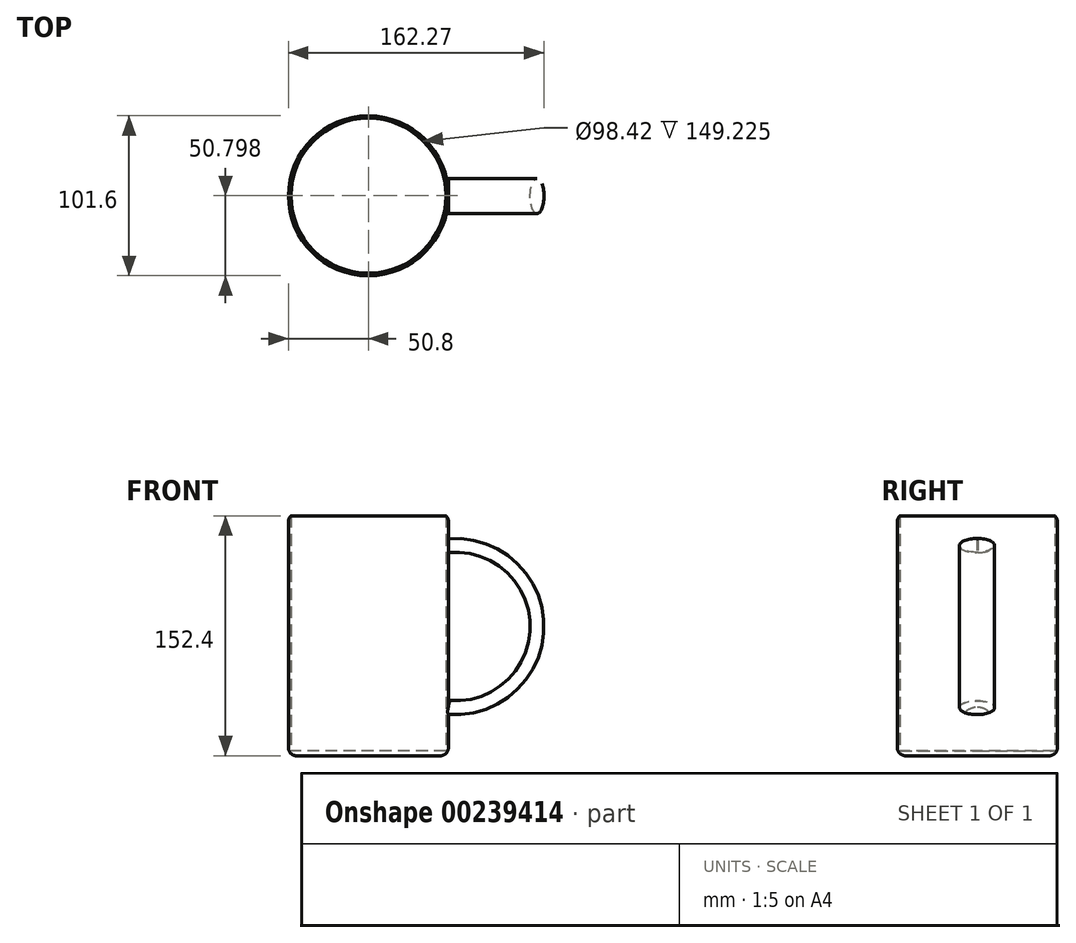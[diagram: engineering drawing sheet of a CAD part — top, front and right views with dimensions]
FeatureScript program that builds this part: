
annotation { "Feature Type Name" : "Feature", "Feature Type Description" : "" }
export const myFeature = defineFeature(function(context is Context, id is Id, definition is map)
    precondition{}
    {
        {
            var Q0;
            Q0=qCreatedBy(makeId("Top.planeOp"),FACE);
            var sketch = newSketch(context, id + "F0", { "sketchPlane" : qUnion([Q0])});
            skCircle(sketch, "E0", {"center": v(-50.8, 0.22) * mm, "radius": 50.8 * mm});
            skPoint(sketch, "E0.first.point", {"position": v(0, 0) * mm});
            skPoint(sketch, "E0.second.point", {"position": v(-101.53, -2.37) * mm});
            skPoint(sketch, "E0.third.point", {"position": v(-78.18, -42.57) * mm});
            skCircle(sketch, "E1", {"center": v(-50.8, 0.22) * mm, "radius": 49.21 * mm});
            skSolve(sketch);
        }
        {
            var Q0;
            Q0 = qSketchRegion(id + "F0", true);
            extrude(context, id + "F1", {"entities" : qUnion([Q0]), "depth" : 152.4 * mm});
        }
        {
            var Q0;
            Q0=makeQuery(id+"F0.imprint","IMPRINT",FACE,{"disambiguationData":[TD([[makeQuery(id+"F0.imprint","IMPRINT",EDGE,{"derivedFrom":sQuery(id+"F0.wireOp",EDGE,"E1")}),1.0]])]});
            extrude(context, id + "F2", {"entities" : qUnion([Q0]), "operationType" : NewBodyOperationType.ADD, "depth" : 3.17 * mm});
        }
        {
            var Q0;
            Q0=qCreatedBy(makeId("Right.planeOp"),FACE);
            var sketch = newSketch(context, id + "F3", { "sketchPlane" : qUnion([Q0])});
            skEllipse(sketch, "E2", {"center": v(0, 133.4) * mm, "majorRadius": 11.13 * mm, "minorRadius": 4.4 * mm, "majorAxis": v(1, 0)});
            skEllipse(sketch, "E3", {"center": v(0.27, 30.77) * mm, "majorRadius": 11.13 * mm, "minorRadius": 4.4 * mm, "majorAxis": v(1, 0)});
            skSolve(sketch);
        }
        {
            var Q0;
            Q0=qCreatedBy(makeId("Front.planeOp"),FACE);
            var sketch = newSketch(context, id + "F4", { "sketchPlane" : qUnion([Q0])});
            skArc(sketch, "E4", {"start": v(0, 31.04) * mm, "mid": v(56.02, 82.09) * mm, "end": v(0, 133.13) * mm});
            skSolve(sketch);
        }
        {
            var Q0;
            Q0=makeQuery(id+"F3.imprint","IMPRINT",FACE,{"disambiguationData":[TD([[makeQuery(id+"F3.imprint","IMPRINT",EDGE,{"derivedFrom":sQuery(id+"F3.wireOp",EDGE,"E2")}),1.0]])]});
            var Q1;
            Q1=sQuery(id+"F4.wireOp",EDGE,"E4");
            sweep(context, id + "F5", {"operationType" : NewBodyOperationType.ADD, "profiles" : qUnion([Q0]), "path" : qUnion([Q1])});
        }
        {
            var Q0;
            Q0=makeQuery(id+"F1.opExtrude","CAP_EDGE",EDGE,{"disambiguationData":[OSD([sQuery(id+"F0.wireOp",EDGE,"E0")])],"isStart":false});
            fillet(context, id + "F6", {"entities" : qUnion([Q0]), "radius" : 5.08 * mm, "tangentPropagation" : true, "allowEdgeOverflow" : false});
        }
        {
            var Q0;
            Q0=makeQuery(id+"F1.opExtrude","CAP_EDGE",EDGE,{"disambiguationData":[OSD([sQuery(id+"F0.wireOp",EDGE,"E0")])],"isStart":true});
            fillet(context, id + "F7", {"entities" : qUnion([Q0]), "radius" : 5.08 * mm, "tangentPropagation" : true, "allowEdgeOverflow" : false});
        }
    });
